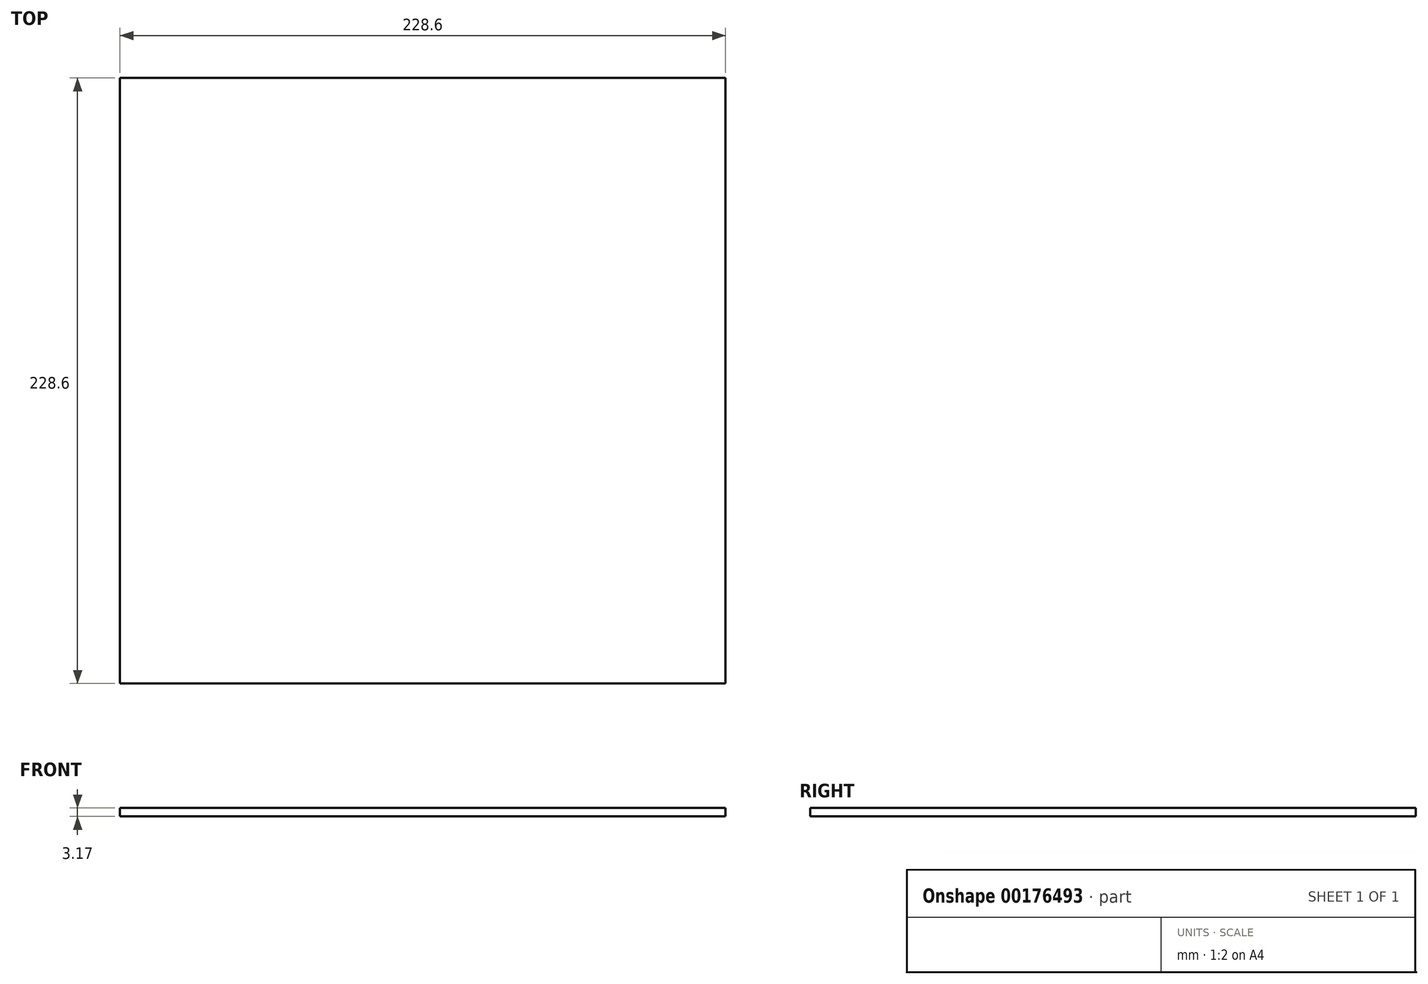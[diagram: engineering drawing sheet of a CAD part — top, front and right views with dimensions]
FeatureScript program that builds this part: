
annotation { "Feature Type Name" : "Feature", "Feature Type Description" : "" }
export const myFeature = defineFeature(function(context is Context, id is Id, definition is map)
    precondition{}
    {
        {
            var Q0;
            Q0=qCreatedBy(makeId("Top.planeOp"),FACE);
            var sketch = newSketch(context, id + "F0", { "sketchPlane" : qUnion([Q0])});
            skLineSegment(sketch, "E0.bottom", {"start": v(114.3, 114.3) * mm, "end": v(-114.3, 114.3) * mm});
            skLineSegment(sketch, "E0.top", {"start": v(114.3, -114.3) * mm, "end": v(-114.3, -114.3) * mm});
            skLineSegment(sketch, "E0.left", {"start": v(114.3, 114.3) * mm, "end": v(114.3, -114.3) * mm});
            skLineSegment(sketch, "E0.right", {"start": v(-114.3, 114.3) * mm, "end": v(-114.3, -114.3) * mm});
            skPoint(sketch, "E0.middle", {"position": v(0, 0) * mm});
            skSolve(sketch);
        }
        {
            var Q0;
            Q0 = qSketchRegion(id + "F0", true);
            extrude(context, id + "F1", {"entities" : qUnion([Q0]), "depth" : 3.17 * mm});
        }
    });
